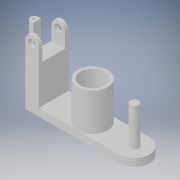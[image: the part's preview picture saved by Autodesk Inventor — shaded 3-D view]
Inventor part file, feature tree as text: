
AUTODESK INVENTOR PART (.ipt)
format: ipt  version: 2019 (Build 230136000, 136)  size: 194,048 bytes
history: native  units: in
note: dims shown in document units (in); Inventor stores cm internally (conversion verified against a paired STEP export)
features: extrude x7, sketch x7, fillet x1
ambient origin geometry x8: Origin, YZ Plane, XZ Plane, XY Plane, X Axis, Y Axis, Z Axis, Center Point
bodies: Solid1 (feature_tree)
feature tree (15):
  extrude  "Extrusion1"  Depth=0.1969in
  sketch  "Sketch2"  dims[d6=0.1772in d7=0.1969in]
  extrude  "Extrusion5"  Depth=0.1969in
  extrude  "Extrusion6"  Depth=0.3543in
  extrude  "Extrusion7"  Depth=0.7874in
  extrude  "Extrusion10"  Depth=0.7874in
  extrude  "Extrusion11"  Depth=0.3937in
  extrude  "Extrusion12"  Depth=0.3937in
  fillet  "Fillet4"  Radius=0.5984in
  sketch  "Sketch1"  dims[d0=1.5748in d2=0.1969in]
  sketch  "Sketch7"  dims[d8=0.3543in d9=2.126in]
  sketch  "Sketch9"  dims[d10=0.7874in d11=0.0in d12=0.1181in]
  sketch  "Sketch12"  dims[d13=0.2559in d14=0.7874in]
  sketch  "Sketch13"  dims[d16=1.0236in d19=0.3937in]
  sketch  "Sketch14"  dims[d20=0.2205in d21=0.3937in d22=0.5984in d40=0.5512in d41=0.5512in d42=0.5906in d43=0.5512in d44=0.0in d47=1.2795in d48=0.9843in d49=0.0in d50=0.6299in d51=1.2205in d52=0.0in d65=0.1969in d66=0.0in d67=0.0in d68=0.0787in d69=0.1969in d70=1.7717in d71=0.0in d72=0.1575in d73=0.3937in d74=0.7874in d75=0.0787in d76=1.1811in d77=0.0in d78=0.0787in]
